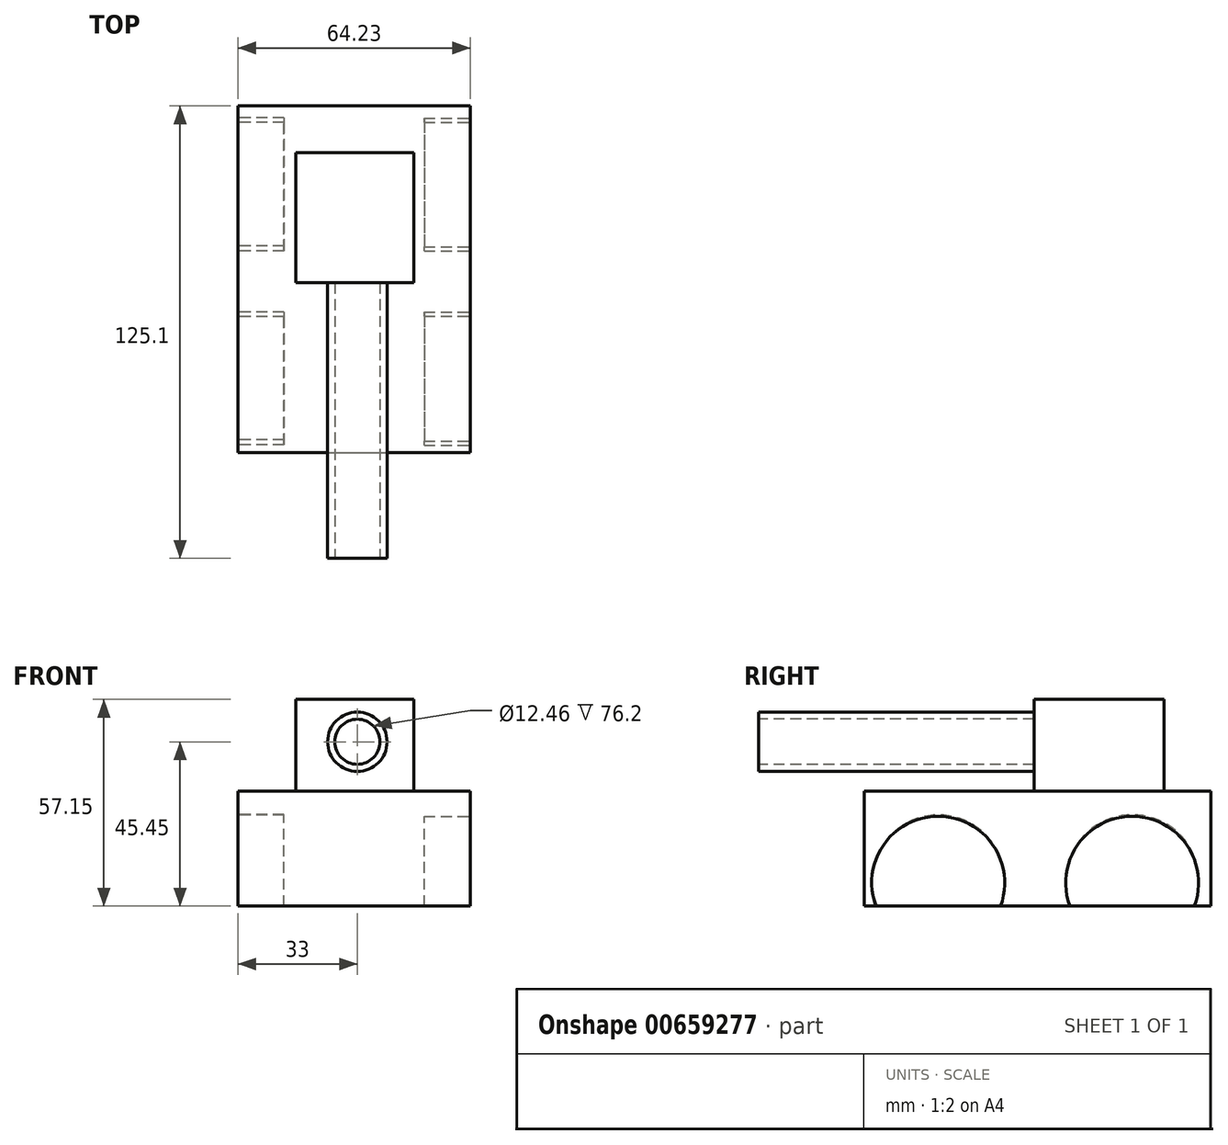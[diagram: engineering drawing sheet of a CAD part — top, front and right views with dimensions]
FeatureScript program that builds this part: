
annotation { "Feature Type Name" : "Feature", "Feature Type Description" : "" }
export const myFeature = defineFeature(function(context is Context, id is Id, definition is map)
    precondition{}
    {
        {
            var Q0;
            Q0=qCreatedBy(makeId("Top.planeOp"),FACE);
            var sketch = newSketch(context, id + "F0", { "sketchPlane" : qUnion([Q0])});
            skLineSegment(sketch, "E0.bottom", {"start": v(-33, 45.23) * mm, "end": v(31.23, 45.23) * mm});
            skLineSegment(sketch, "E0.top", {"start": v(-33, -50.56) * mm, "end": v(31.23, -50.56) * mm});
            skLineSegment(sketch, "E0.left", {"start": v(-33, 45.23) * mm, "end": v(-33, -50.56) * mm});
            skLineSegment(sketch, "E0.right", {"start": v(31.23, 45.23) * mm, "end": v(31.23, -50.56) * mm});
            skSolve(sketch);
        }
        {
            var Q0;
            Q0=makeQuery(id+"F0.imprint","IMPRINT",FACE,{"disambiguationData":[TD([[makeQuery(id+"F0.imprint","IMPRINT",EDGE,{"derivedFrom":sQuery(id+"F0.wireOp",EDGE,"E0.bottom")}),-1.0]])]});
            extrude(context, id + "F1", {"entities" : qUnion([Q0]), "depth" : 31.75 * mm, "offsetDistance" : 25.4 * mm});
        }
        {
            var Q0;
            Q0=makeQuery(id+"F1.opExtrude","SWEPT_FACE",FACE,{"disambiguationData":[OSD([sQuery(id+"F0.wireOp",EDGE,"E0.right")])]});
            var sketch = newSketch(context, id + "F2", { "sketchPlane" : qUnion([Q0])});
            skCircle(sketch, "E1", {"center": v(23.5, 6.43) * mm, "radius": 18.38 * mm});
            skArc(sketch, "E2", {"start": v(-13.58, -1.57) * mm, "mid": v(-30, 24.83) * mm, "end": v(-46.86, -1.29) * mm});
            skArc(sketch, "E3", {"start": v(-46.86, -1.29) * mm, "mid": v(-42.64, -7.09) * mm, "end": v(-36.53, -10.83) * mm});
            skArc(sketch, "E4", {"start": v(-36.53, -10.83) * mm, "mid": v(-34.83, -11.37) * mm, "end": v(-33.09, -11.74) * mm});
            skArc(sketch, "E5", {"start": v(-33.09, -11.74) * mm, "mid": v(-21.65, -9.9) * mm, "end": v(-13.58, -1.57) * mm});
            skSolve(sketch);
        }
        {
            var Q0;
            Q0=makeQuery(id+"F1.opExtrude","SWEPT_FACE",FACE,{"disambiguationData":[OSD([sQuery(id+"F0.wireOp",EDGE,"E0.left")])]});
            var sketch = newSketch(context, id + "F3", { "sketchPlane" : qUnion([Q0])});
            skCircle(sketch, "E6", {"center": v(-23.57, 6.85) * mm, "radius": 18.41 * mm});
            skCircle(sketch, "E7", {"center": v(30.08, 6.85) * mm, "radius": 18.35 * mm});
            skSolve(sketch);
        }
        {
            var Q0;
            {var subQ0=sQuery(id+"F2.wireOp",EDGE,"E2");var subQ1=makeQuery(id+"F1.opExtrude","CAP_EDGE",EDGE,{"disambiguationData":[OSD([sQuery(id+"F0.wireOp",EDGE,"E0.right")])],"isStart":true});var subQ2=makeQuery(id+"F2.imprint","INTERSECT",VERTEX,{"disambiguationData":[OD(0.0)],"derivedFrom":[subQ1,subQ0]});Q0=makeQuery(id+"F2.imprint","IMPRINT",FACE,{"disambiguationData":[TD([[makeQuery(id+"F2.imprint","IMPRINT",EDGE,{"disambiguationData":[TD([[subQ2,-1.0]])],"derivedFrom":subQ0}),1.0]])]});}
            var Q1;
            {var subQ0=sQuery(id+"F2.wireOp",EDGE,"E1");var subQ1=makeQuery(id+"F1.opExtrude","CAP_EDGE",EDGE,{"disambiguationData":[OSD([sQuery(id+"F0.wireOp",EDGE,"E0.right")])],"isStart":true});var subQ2=makeQuery(id+"F2.imprint","INTERSECT",VERTEX,{"disambiguationData":[OD(0.0)],"derivedFrom":[subQ1,subQ0]});Q1=makeQuery(id+"F2.imprint","IMPRINT",FACE,{"disambiguationData":[TD([[makeQuery(id+"F2.imprint","IMPRINT",EDGE,{"disambiguationData":[TD([[subQ2,-1.0]])],"derivedFrom":subQ0}),1.0]])]});}
            extrude(context, id + "F4", {"entities" : qUnion([Q0, Q1]), "operationType" : NewBodyOperationType.REMOVE, "oppositeDirection" : true, "depth" : 12.7 * mm, "offsetDistance" : 25.4 * mm});
        }
        {
            var Q0;
            {var subQ0=sQuery(id+"F3.wireOp",EDGE,"E6");var subQ1=makeQuery(id+"F1.opExtrude","CAP_EDGE",EDGE,{"disambiguationData":[OSD([sQuery(id+"F0.wireOp",EDGE,"E0.left")])],"isStart":true});var subQ2=makeQuery(id+"F3.imprint","INTERSECT",VERTEX,{"disambiguationData":[OD(0.0)],"derivedFrom":[subQ1,subQ0]});Q0=makeQuery(id+"F3.imprint","IMPRINT",FACE,{"disambiguationData":[TD([[makeQuery(id+"F3.imprint","IMPRINT",EDGE,{"disambiguationData":[TD([[subQ2,1.0]])],"derivedFrom":subQ0}),1.0]])]});}
            var Q1;
            {var subQ0=sQuery(id+"F3.wireOp",EDGE,"E7");var subQ1=makeQuery(id+"F1.opExtrude","CAP_EDGE",EDGE,{"disambiguationData":[OSD([sQuery(id+"F0.wireOp",EDGE,"E0.left")])],"isStart":true});var subQ2=makeQuery(id+"F3.imprint","INTERSECT",VERTEX,{"disambiguationData":[OD(0.0)],"derivedFrom":[subQ1,subQ0]});Q1=makeQuery(id+"F3.imprint","IMPRINT",FACE,{"disambiguationData":[TD([[makeQuery(id+"F3.imprint","IMPRINT",EDGE,{"disambiguationData":[TD([[subQ2,-1.0]])],"derivedFrom":subQ0}),1.0]])]});}
            extrude(context, id + "F5", {"entities" : qUnion([Q0, Q1]), "operationType" : NewBodyOperationType.REMOVE, "oppositeDirection" : true, "depth" : 12.7 * mm, "offsetDistance" : 25.4 * mm});
        }
        {
            var Q0;
            Q0=makeQuery(id+"F1.opExtrude","CAP_FACE",FACE,{"disambiguationData":[OSD([sQuery(id+"F0.wireOp",EDGE,"E0.bottom"),sQuery(id+"F0.wireOp",EDGE,"E0.top"),sQuery(id+"F0.wireOp",EDGE,"E0.left"),sQuery(id+"F0.wireOp",EDGE,"E0.right")])],"isStart":false});
            var sketch = newSketch(context, id + "F6", { "sketchPlane" : qUnion([Q0])});
            skLineSegment(sketch, "E8.bottom", {"start": v(-17, 32.34) * mm, "end": v(15.67, 32.34) * mm});
            skLineSegment(sketch, "E8.top", {"start": v(-17, -3.67) * mm, "end": v(15.67, -3.67) * mm});
            skLineSegment(sketch, "E8.left", {"start": v(-17, 32.34) * mm, "end": v(-17, -3.67) * mm});
            skLineSegment(sketch, "E8.right", {"start": v(15.67, 32.34) * mm, "end": v(15.67, -3.67) * mm});
            skSolve(sketch);
        }
        {
            var Q0;
            Q0=makeQuery(id+"F6.imprint","IMPRINT",FACE,{"disambiguationData":[TD([[makeQuery(id+"F6.imprint","IMPRINT",EDGE,{"derivedFrom":sQuery(id+"F6.wireOp",EDGE,"E8.bottom")}),-1.0]])]});
            extrude(context, id + "F7", {"entities" : qUnion([Q0]), "operationType" : NewBodyOperationType.ADD, "depth" : 25.4 * mm, "offsetDistance" : 25.4 * mm});
        }
        {
            var Q0;
            Q0=makeQuery(id+"F7.opExtrude","SWEPT_FACE",FACE,{"disambiguationData":[OSD([sQuery(id+"F6.wireOp",EDGE,"E8.top")])]});
            var sketch = newSketch(context, id + "F8", { "sketchPlane" : qUnion([Q0])});
            skCircle(sketch, "E9", {"center": v(0, 45.45) * mm, "radius": 8.22 * mm});
            skSolve(sketch);
        }
        {
            var Q0;
            Q0=makeQuery(id+"F8.imprint","IMPRINT",FACE,{"disambiguationData":[TD([[makeQuery(id+"F8.imprint","IMPRINT",EDGE,{"derivedFrom":sQuery(id+"F8.wireOp",EDGE,"E9")}),1.0]])]});
            extrude(context, id + "F9", {"entities" : qUnion([Q0]), "operationType" : NewBodyOperationType.ADD, "depth" : 76.2 * mm, "offsetDistance" : 25.4 * mm});
        }
        {
            var Q0;
            Q0=makeQuery(id+"F9.opExtrude","CAP_FACE",FACE,{"disambiguationData":[OSD([sQuery(id+"F8.wireOp",EDGE,"E9")])],"isStart":false});
            var sketch = newSketch(context, id + "F10", { "sketchPlane" : qUnion([Q0])});
            skCircle(sketch, "E10", {"center": v(0, 45.45) * mm, "radius": 6.23 * mm});
            skSolve(sketch);
        }
        {
            var Q0;
            Q0=makeQuery(id+"F10.imprint","IMPRINT",FACE,{"disambiguationData":[TD([[makeQuery(id+"F10.imprint","IMPRINT",EDGE,{"derivedFrom":sQuery(id+"F10.wireOp",EDGE,"E10")}),1.0]])]});
            extrude(context, id + "F11", {"entities" : qUnion([Q0]), "operationType" : NewBodyOperationType.REMOVE, "oppositeDirection" : true, "depth" : 76.2 * mm, "offsetDistance" : 25.4 * mm});
        }
    });
